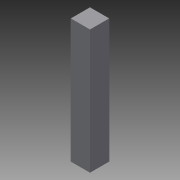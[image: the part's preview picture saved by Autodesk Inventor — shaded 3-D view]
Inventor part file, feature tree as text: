
AUTODESK INVENTOR PART (.ipt)
format: ipt  version: 2015 (Build 190159000, 159)  size: 67,584 bytes
history: native  units: in
note: dims shown in document units (in); Inventor stores cm internally (conversion verified against a paired STEP export)
features: extrude x1, sketch x1
ambient origin geometry x8: Origin, YZ Plane, XZ Plane, XY Plane, X Axis, Y Axis, Z Axis, Center Point
bodies: Solid1 (feature_tree)
feature tree (2):
  extrude  "Extrusion1"  Depth=0.75in
  sketch  "Sketch1"  dims[d0=0.75in d1=0.75in d2=4.85in d3=0.0in]
